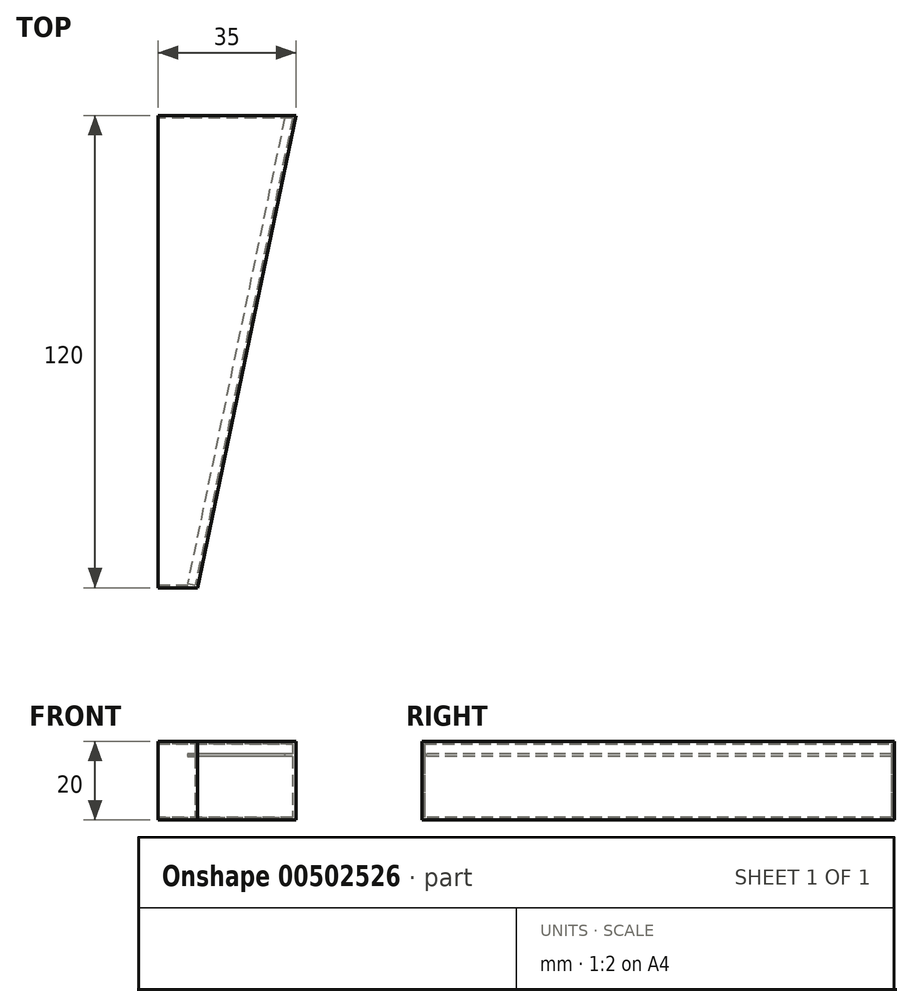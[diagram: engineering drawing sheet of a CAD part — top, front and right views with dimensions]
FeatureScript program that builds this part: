
annotation { "Feature Type Name" : "Feature", "Feature Type Description" : "" }
export const myFeature = defineFeature(function(context is Context, id is Id, definition is map)
    precondition{}
    {
        {
            var Q0;
            Q0=qCreatedBy(makeId("Top.planeOp"),FACE);
            var sketch = newSketch(context, id + "F0", { "sketchPlane" : qUnion([Q0])});
            skLineSegment(sketch, "E0", {"start": v(-12.5, 80) * mm, "end": v(-12.5, -40) * mm});
            skLineSegment(sketch, "E1", {"start": v(-12.5, -40) * mm, "end": v(-2.5, -40) * mm});
            skLineSegment(sketch, "E2", {"start": v(-2.5, -40) * mm, "end": v(22.5, 80) * mm});
            skLineSegment(sketch, "E3", {"start": v(22.5, 80) * mm, "end": v(-12.5, 80) * mm});
            skSolve(sketch);
        }
        {
            var Q0;
            Q0=makeQuery(id+"F0.imprint","IMPRINT",FACE,{"disambiguationData":[TD([[makeQuery(id+"F0.imprint","IMPRINT",EDGE,{"derivedFrom":sQuery(id+"F0.wireOp",EDGE,"E0")}),1.0]])]});
            extrude(context, id + "F1", {"entities" : qUnion([Q0]), "depth" : 20 * mm});
        }
        {
            var Q0;
            Q0=makeQuery(id+"F1.opExtrude","SWEPT_FACE",FACE,{"disambiguationData":[OSD([sQuery(id+"F0.wireOp",EDGE,"E0")])]});
            shell(context, id + "F2", {"entities" : qUnion([Q0]), "thickness" : 0.7 * mm});
        }
        {
            var Q0;
            Q0=makeQuery(id+"F2.opShell","OFFSET_FACE",FACE,{"disambiguationData":[OSD([sQuery(id+"F0.wireOp",EDGE,"E2")])]});
            var sketch = newSketch(context, id + "F3", { "sketchPlane" : qUnion([Q0])});
            skLineSegment(sketch, "E4.bottom", {"start": v(-82.05, 16.8) * mm, "end": v(39.1, 16.8) * mm});
            skLineSegment(sketch, "E4.top", {"start": v(-82.05, 16.1) * mm, "end": v(39.1, 16.1) * mm});
            skLineSegment(sketch, "E4.left", {"start": v(-82.05, 16.8) * mm, "end": v(-82.05, 16.1) * mm});
            skLineSegment(sketch, "E4.right", {"start": v(39.1, 16.8) * mm, "end": v(39.1, 16.1) * mm});
            skSolve(sketch);
        }
        {
            var Q0;
            Q0=makeQuery(id+"F3.imprint","IMPRINT",FACE,{"disambiguationData":[TD([[makeQuery(id+"F3.imprint","IMPRINT",EDGE,{"derivedFrom":sQuery(id+"F3.wireOp",EDGE,"E4.bottom")}),-1.0]])]});
            extrude(context, id + "F4", {"entities" : qUnion([Q0]), "operationType" : NewBodyOperationType.ADD, "depth" : 2 * mm});
        }
    });
